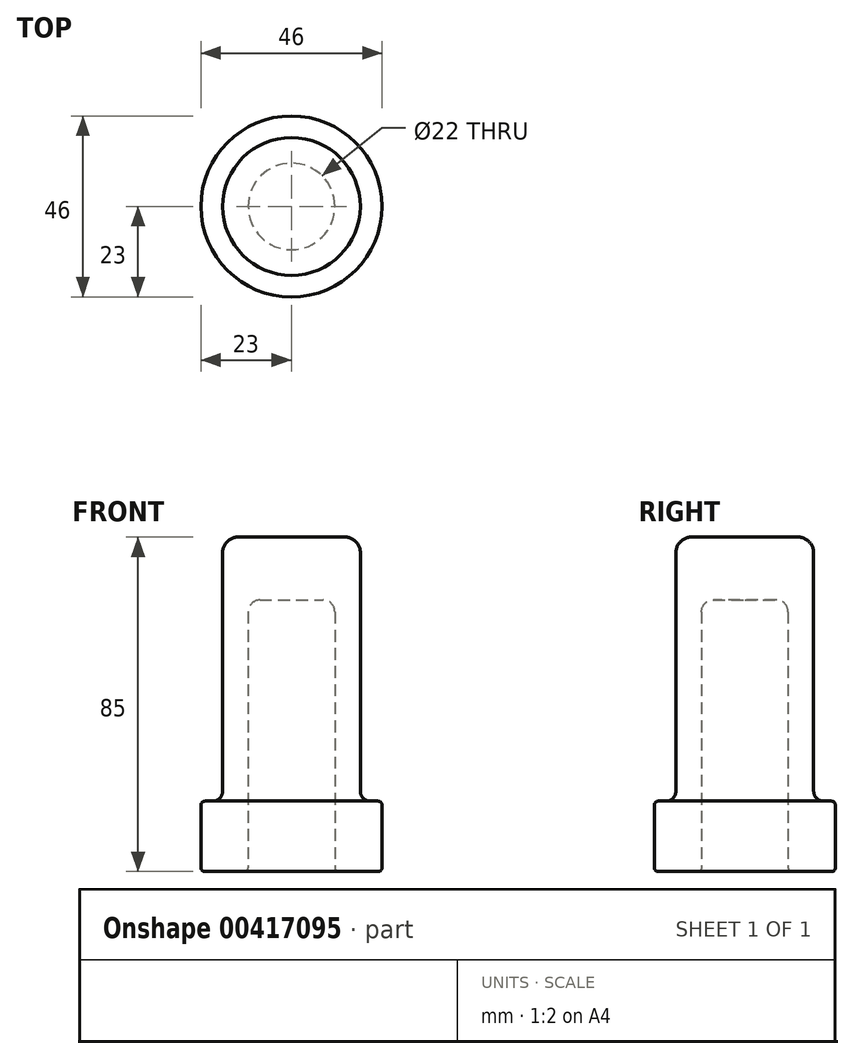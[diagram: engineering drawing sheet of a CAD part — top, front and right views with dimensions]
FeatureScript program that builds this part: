
annotation { "Feature Type Name" : "Feature", "Feature Type Description" : "" }
export const myFeature = defineFeature(function(context is Context, id is Id, definition is map)
    precondition{}
    {
        {
            var Q0;
            Q0=qCreatedBy(makeId("Front.planeOp"),FACE);
            var sketch = newSketch(context, id + "F0", { "sketchPlane" : qUnion([Q0])});
            skLineSegment(sketch, "E0.bottom", {"start": v(-11, 0) * mm, "end": v(-18, 0) * mm});
            skLineSegment(sketch, "E0.top", {"start": v(-11, 52.1) * mm, "end": v(-17.5, 52.1) * mm});
            skLineSegment(sketch, "E0.left", {"start": v(-11, 0) * mm, "end": v(-11, 48.1) * mm});
            skLineSegment(sketch, "E0.right", {"start": v(-17.5, 2.5) * mm, "end": v(-17.5, 52.1) * mm});
            skLineSegment(sketch, "E1.bottom", {"start": v(-8, 51.1) * mm, "end": v(0, 51.1) * mm});
            skLineSegment(sketch, "E1.top", {"start": v(-13.5, 67.1) * mm, "end": v(0, 67.1) * mm});
            skLineSegment(sketch, "E1.left", {"start": v(-17.5, 52.1) * mm, "end": v(-17.5, 63.1) * mm});
            skLineSegment(sketch, "E1.right", {"start": v(0, 51.1) * mm, "end": v(0, 67.1) * mm});
            skLineSegment(sketch, "E2.bottom", {"start": v(-20, 0) * mm, "end": v(-22, 0) * mm});
            skLineSegment(sketch, "E2.top", {"start": v(-12, -17.9) * mm, "end": v(-22, -17.9) * mm});
            skLineSegment(sketch, "E2.left", {"start": v(-11, 0) * mm, "end": v(-11, -16.9) * mm});
            skLineSegment(sketch, "E2.right", {"start": v(-23, -1) * mm, "end": v(-23, -16.9) * mm});
            skPoint(sketch, "E3.visualSharp", {"position": v(-23, -17.9) * mm});
            skArc(sketch, "E3.filletArc", {"start": v(-23, -16.9) * mm, "mid": v(-22.7, -17.6) * mm, "end": v(-22, -17.9) * mm});
            skPoint(sketch, "E4.visualSharp", {"position": v(-11, -17.9) * mm});
            skArc(sketch, "E4.filletArc", {"start": v(-12, -17.9) * mm, "mid": v(-11.3, -17.6) * mm, "end": v(-11, -16.9) * mm});
            skPoint(sketch, "E5.visualSharp", {"position": v(-23, 0) * mm});
            skArc(sketch, "E5.filletArc", {"start": v(-22, 0) * mm, "mid": v(-22.7, -0.3) * mm, "end": v(-23, -1) * mm});
            skPoint(sketch, "E6.newPointA", {"position": v(-10.52, 0) * mm});
            skPoint(sketch, "E6.newPointB", {"position": v(-17.5, 0.5) * mm});
            skArc(sketch, "E6.filletArc", {"start": v(-20, 0) * mm, "mid": v(-18.23, 0.73) * mm, "end": v(-17.5, 2.5) * mm});
            skPoint(sketch, "E7.visualSharp", {"position": v(-17.5, 67.1) * mm});
            skArc(sketch, "E8.filletArc", {"start": v(-13.5, 67.1) * mm, "mid": v(-16.33, 65.93) * mm, "end": v(-17.5, 63.1) * mm});
            skPoint(sketch, "E9.newPointA", {"position": v(-11, 52.1) * mm});
            skArc(sketch, "E9.filletArc", {"start": v(-8, 51.1) * mm, "mid": v(-10.12, 50.22) * mm, "end": v(-11, 48.1) * mm});
            skLineSegment(sketch, "E10", {"start": v(0, 73.54) * mm, "end": v(0, -54.5) * mm});
            skSolve(sketch);
        }
        {
            var Q0;
            Q0=makeQuery(id+"F0.imprint","IMPRINT",FACE,{"disambiguationData":[TD([[makeQuery(id+"F0.imprint","IMPRINT",EDGE,{"derivedFrom":sQuery(id+"F0.wireOp",EDGE,"E0.left")}),1.0]])]});
            var Q1;
            Q1=sQuery(id+"F0.wireOp",EDGE,"E0.right");
            var Q2;
            Q2=sQuery(id+"F0.wireOp",EDGE,"E1.bottom");
            var Q3;
            Q3=sQuery(id+"F0.wireOp",EDGE,"E1.top");
            var Q4;
            Q4=sQuery(id+"F0.wireOp",EDGE,"E1.left");
            var Q5;
            Q5=sQuery(id+"F0.wireOp",EDGE,"E1.right");
            var Q6;
            Q6=sQuery(id+"F0.wireOp",EDGE,"E0.top");
            var Q7;
            Q7=sQuery(id+"F0.wireOp",EDGE,"E0.left");
            var Q8;
            Q8=sQuery(id+"F0.wireOp",EDGE,"E8.filletArc");
            var Q9;
            Q9=sQuery(id+"F0.wireOp",EDGE,"E0.bottom");
            var Q10;
            Q10=sQuery(id+"F0.wireOp",EDGE,"E6.filletArc");
            var Q11;
            Q11=sQuery(id+"F0.wireOp",EDGE,"E9.filletArc");
            var Q12;
            Q12=sQuery(id+"F0.wireOp",EDGE,"E2.bottom");
            var Q13;
            Q13=sQuery(id+"F0.wireOp",EDGE,"E5.filletArc");
            var Q14;
            Q14=sQuery(id+"F0.wireOp",EDGE,"E2.top");
            var Q15;
            Q15=sQuery(id+"F0.wireOp",EDGE,"E2.left");
            var Q16;
            Q16=sQuery(id+"F0.wireOp",EDGE,"E2.right");
            var Q17;
            Q17=sQuery(id+"F0.wireOp",EDGE,"E3.filletArc");
            var Q18;
            Q18=sQuery(id+"F0.wireOp",EDGE,"E4.filletArc");
            var Q19;
            Q19=sQuery(id+"F0.wireOp",EDGE,"E10");
            revolve(context, id + "F1", {"entities" : qUnion([Q0]), "surfaceEntities" : qUnion([Q1, Q2, Q3, Q4, Q5, Q6, Q7, Q8, Q9, Q10, Q11, Q12, Q13, Q14, Q15, Q16, Q17, Q18]), "axis" : qUnion([Q19]), "revolveType" : RevolveType.ONE_DIRECTION, "oppositeDirection" : true, "angle" : 360 * degree});
        }
    });
